# Revit family: Container_Valve_Assembly-JCI_Sapphire_Plus-(70bar)Novec1230
name_source: partatom
category: Specialty Equipment
revit_build: Autodesk Revit 2017 (Build: 20171027_0315(x64)
units: mm (PartAtom-declared; Revit-internal decimal feet)

## family parameters
Always vertical = Yes
Cut with Voids When Loaded = No
OmniClass Number = 23.29.33.13.11
Part Type = Normal
Room Calculation Point = No
Round Connector Dimension = Use Diameter
Shared = No
Work Plane-Based = Yes

## types (18) — shared parameters
120 Litre = Seamless Steel Cylinder : 120 Litre
15 Litre = Seamless Steel Cylinder : 15 Litre
180 Litre = Seamless Steel Cylinder : 180 Litre
30 Litre = Seamless Steel Cylinder : 30 Litre
45 Litre = Seamless Steel Cylinder : 45 Litre
60 Litre = Seamless Steel Cylinder : 60 Litre
Assembly Code = D4090300
Date Modified = 2018/09/26
Family Version = 1.0
Fire Suppression Agent = 3M™ Novec™ 1230 Fire Protection Fluid
Manufacturer = Johnson Controls, Inc.
Materials = JCI - Metal - Steel - Paint - Red
Model Disclaimer = For More Information Contact JOHNSON CONTROLS
Operating Temperature = 122 °F
Product Documentation Link = http://www.sapphireplus.com
Product Material = JCI - Iron - Gray; JCI - Plastic - Red - Matte
Product Page URL = http://www.sapphireplus.com
Unit Assembly = Sapphire Plus_Container
zero-valued in all types: Default Elevation

## per-type parameters (varying)
| type | ACTUATOR TYPE | Container Type Number | Description | Model | Tank Selection | URL | Weight |
| TPED_45 L_Pneumatic Actuator_ASSEMBLY | ACTUATOR TYPE SELECTOR : Pneumatic Actuator | 45 | Container 45 l TPED | 30370003 | Seamless Steel Cylinder : 45 Litre | http://www.sapphireplus.com | 18.58 lbf |
| TPED_45 L_Manual Actuator_ASSEMBLY | ACTUATOR TYPE SELECTOR : Manual Actuator | 45 | Container 45 l TPED | 30370003 | Seamless Steel Cylinder : 45 Litre | http://www.sapphireplus.com | 18.58 lbf |
| TPED_30 L_Pneumatic Actuator_ASSEMBLY | ACTUATOR TYPE SELECTOR : Pneumatic Actuator | 30 | Container 30 l TPED | 30370002 | Seamless Steel Cylinder : 30 Litre | http://www.sapphireplus.com | 12.16 lbf |
| TPED_30 L_Manual Actuator_ASSEMBLY | ACTUATOR TYPE SELECTOR : Manual Actuator | 30 | Container 30 l TPED | 30370002 | Seamless Steel Cylinder : 30 Litre | http://www.sapphireplus.com | 12.16 lbf |
| TPED_180 L_Pneumatic Actuator_ASSEMBLY | ACTUATOR TYPE SELECTOR : Pneumatic Actuator | 180 | Container 180 l TPED | 30370006 | Seamless Steel Cylinder : 180 Litre | http://www.sapphireplus.com | 70.48 lbf |
| TPED_180 L_Manual Actuator_ASSEMBLY | ACTUATOR TYPE SELECTOR : Manual Actuator | 180 | Container 180 l TPED | 30370006 | Seamless Steel Cylinder : 180 Litre | http://www.sapphireplus.com | 70.48 lbf |
| TPED_15 L_Pneumatic Actuator_ASSEMBLY | ACTUATOR TYPE SELECTOR : Pneumatic Actuator | 15 | Container 15 l TPED | 30370001 | Seamless Steel Cylinder : 15 Litre | http://www.sapphireplus.com | 7.58 lbf |
| TPED_15 L_Manual Actuator_ASSEMBLY | ACTUATOR TYPE SELECTOR : Manual Actuator | 15 | Container 15 l TPED | 30370001 | Seamless Steel Cylinder : 15 Litre | http://www.sapphireplus.com | 7.58 lbf |
| TPED_120 L_Manual Actuator_ASSEMBLY | ACTUATOR TYPE SELECTOR : Manual Actuator | 120 | Container 120 l TPED | 30370011 | Seamless Steel Cylinder : 120 Litre | http://www.sapphireplus.com | 46.59 lbf |
| TPED_120 L_Pneumatic Actuator_ASSEMBLY | ACTUATOR TYPE SELECTOR : Pneumatic Actuator | 120 | Container 120 l TPED | 30370011 | Seamless Steel Cylinder : 120 Litre | http://www.sapphireplus.com | 46.59 lbf |
| TPED_60 L_Pneumatic Actuator_ASSEMBLY | ACTUATOR TYPE SELECTOR : Pneumatic Actuator | 60 | Container 60 l TPED | 30370004 | Seamless Steel Cylinder : 60 Litre | https://www.ansul.com | 24.78 lbf |
| TPED_60 L_Manual Actuator_ASSEMBLY | ACTUATOR TYPE SELECTOR : Manual Actuator | 60 | Container 60 l TPED | 30370004 | Seamless Steel Cylinder : 60 Litre | https://www.ansul.com | 24.78 lbf |
| TPED_120 L_Manual Pneumatic Actuator_ASSEMBLY | ACTUATOR TYPE SELECTOR : Manual Pneumatic Actuator | 120 | Container 120 l TPED | 30370011 | Seamless Steel Cylinder : 120 Litre | http://www.sapphireplus.com | 46.59 lbf |
| TPED_60 L_Manual Pneumatic Actuator_ASSEMBLY | ACTUATOR TYPE SELECTOR : Manual Pneumatic Actuator | 60 | Container 60 l TPED | 30370004 | Seamless Steel Cylinder : 60 Litre | https://www.ansul.com | 24.78 lbf |
| TPED_45 L_Manual Pneumatic Actuator_ASSEMBLY | ACTUATOR TYPE SELECTOR : Manual Pneumatic Actuator | 45 | Container 45 l TPED | 30370003 | Seamless Steel Cylinder : 45 Litre | http://www.sapphireplus.com | 18.58 lbf |
| TPED_30 L_Manual Pneumatic Actuator_ASSEMBLY | ACTUATOR TYPE SELECTOR : Manual Pneumatic Actuator | 30 | Container 30 l TPED | 30370002 | Seamless Steel Cylinder : 30 Litre | http://www.sapphireplus.com | 12.16 lbf |
| TPED_180 L_Manual Pneumatic Actuator_ASSEMBLY | ACTUATOR TYPE SELECTOR : Manual Pneumatic Actuator | 180 | Container 180 l TPED | 30370006 | Seamless Steel Cylinder : 180 Litre | http://www.sapphireplus.com | 70.48 lbf |
| TPED_15 L_Manual Pneumatic Actuator_ASSEMBLY | ACTUATOR TYPE SELECTOR : Manual Pneumatic Actuator | 15 | Container 15 l TPED | 30370001 | Seamless Steel Cylinder : 15 Litre | http://www.sapphireplus.com | 7.58 lbf |

## geometry (parser evidence)
native form markers: Sweep x33
no freeform markers — native parametric forms only
